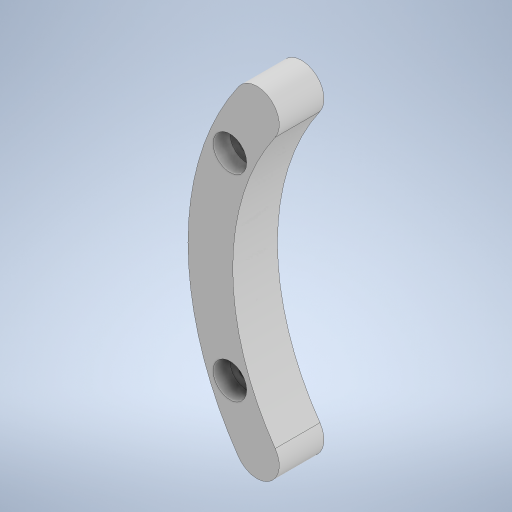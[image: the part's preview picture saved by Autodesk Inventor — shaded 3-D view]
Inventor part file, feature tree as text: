
AUTODESK INVENTOR PART (.ipt)
format: ipt  version: 2024.3 (Build 283343000, 343)  size: 275,456 bytes
history: native  units: mm
features: extrude x2, sketch x2, other x1, fillet x1
ambient origin geometry x8: Origin, YZ Plane, XZ Plane, XY Plane, X Axis, Y Axis, Z Axis, Center Point
bodies: Body1 (feature_tree)
feature tree (6):
  other  "ソリッド1"
  extrude  "押し出し1"  Depth=92.0mm
  fillet  "フィレット1"  Radius=100.0mm
  extrude  "押し出し2"  Depth=84.0mm
  sketch  "スケッチ1"
  sketch  "スケッチ2"
